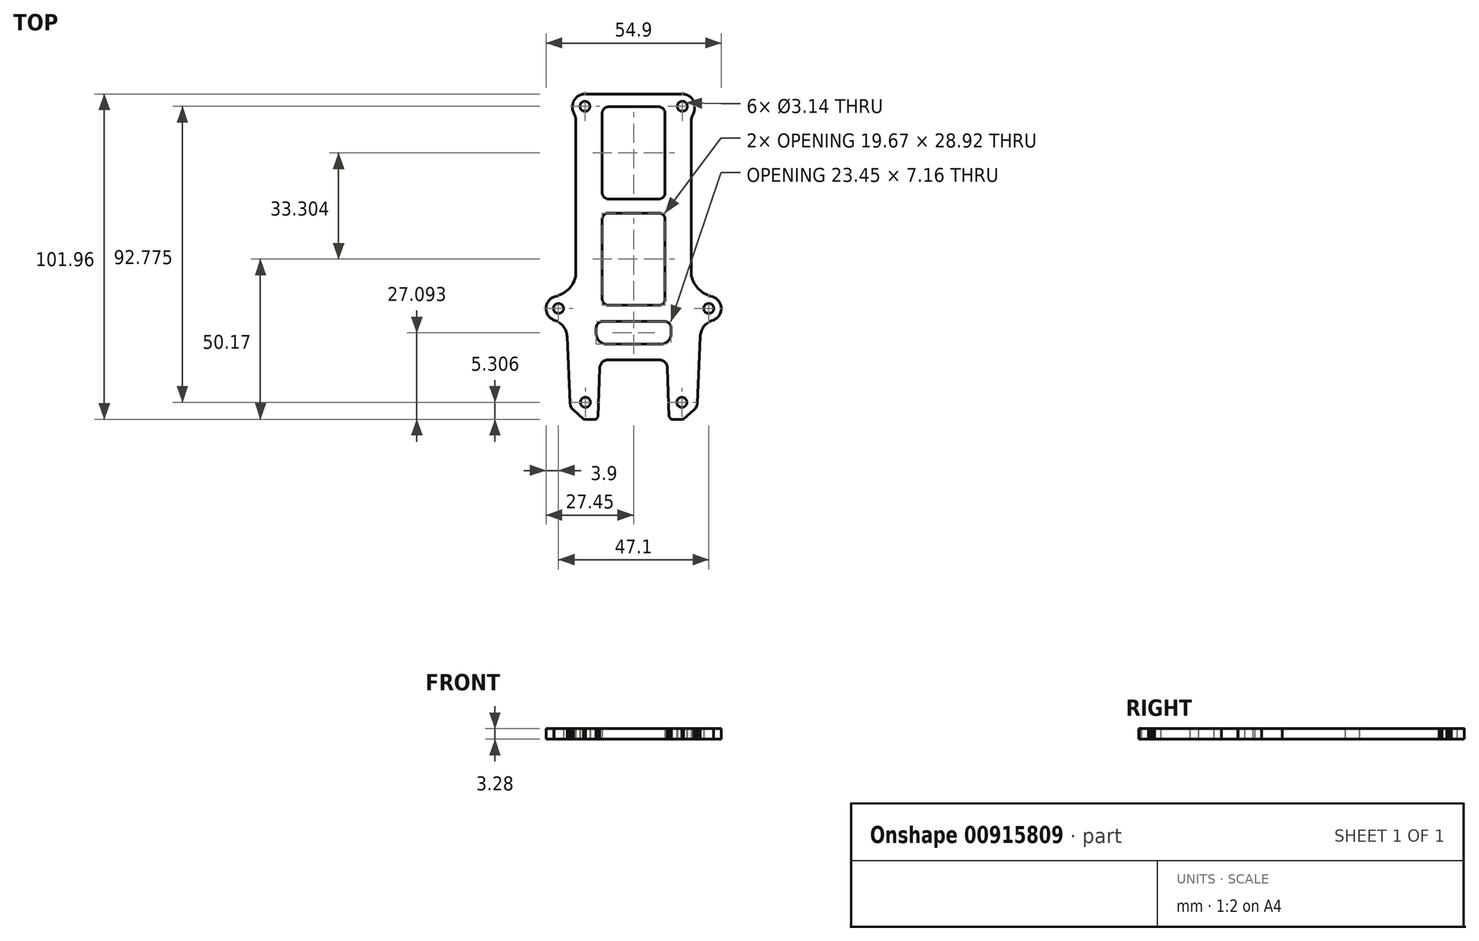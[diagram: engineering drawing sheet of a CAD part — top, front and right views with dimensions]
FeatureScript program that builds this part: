
annotation { "Feature Type Name" : "Feature", "Feature Type Description" : "" }
export const myFeature = defineFeature(function(context is Context, id is Id, definition is map)
    precondition{}
    {
        {
            var Q0;
            Q0=qCreatedBy(makeId("Top.planeOp"),FACE);
            var sketch = newSketch(context, id + "F0", { "sketchPlane" : qUnion([Q0])});
            skLineSegment(sketch, "E0.left", {"start": v(-27.58, 80.06) * mm, "end": v(-27.58, -59.75) * mm});
            skLineSegment(sketch, "E1.bottom", {"start": v(-11.99, 35.27) * mm, "end": v(0, 35.27) * mm});
            skLineSegment(sketch, "E1.top", {"start": v(-11.99, -8.8) * mm, "end": v(0, -8.8) * mm});
            skLineSegment(sketch, "E1.left", {"start": v(-14.99, 32.27) * mm, "end": v(-14.99, -5.8) * mm});
            skPoint(sketch, "E2.visualSharp", {"position": v(-14.99, 36.07) * mm});
            skArc(sketch, "E2.filletArc", {"start": v(-11.99, 35.27) * mm, "mid": v(-14.1, 34.39) * mm, "end": v(-14.99, 32.27) * mm});
            skPoint(sketch, "E3.visualSharp", {"position": v(-14.99, -8.8) * mm});
            skArc(sketch, "E3.filletArc", {"start": v(-14.99, -5.8) * mm, "mid": v(-14.1, -7.92) * mm, "end": v(-11.99, -8.8) * mm});
            skLineSegment(sketch, "E4.bottom", {"start": v(-11.99, 86.01) * mm, "end": v(0, 86.01) * mm});
            skLineSegment(sketch, "E4.top", {"start": v(-11.99, 41.94) * mm, "end": v(0, 41.94) * mm});
            skLineSegment(sketch, "E4.left", {"start": v(-14.99, 83.01) * mm, "end": v(-14.99, 44.94) * mm});
            skPoint(sketch, "E5.visualSharp", {"position": v(-14.99, 86.01) * mm});
            skArc(sketch, "E5.filletArc", {"start": v(-11.99, 86.01) * mm, "mid": v(-14.1, 85.13) * mm, "end": v(-14.99, 83.01) * mm});
            skPoint(sketch, "E6.visualSharp", {"position": v(-14.99, 41.94) * mm});
            skArc(sketch, "E6.filletArc", {"start": v(-14.99, 44.94) * mm, "mid": v(-14.1, 42.82) * mm, "end": v(-11.99, 41.94) * mm});
            skLineSegment(sketch, "E7.bottom", {"start": v(-12.87, -27.38) * mm, "end": v(0, -27.38) * mm});
            skLineSegment(sketch, "E7.top", {"start": v(-14.87, -16.48) * mm, "end": v(0, -16.48) * mm});
            skLineSegment(sketch, "E7.left", {"start": v(-17.87, -22.38) * mm, "end": v(-17.87, -19.48) * mm});
            skPoint(sketch, "E8.visualSharp", {"position": v(-17.87, -16.48) * mm});
            skArc(sketch, "E8.filletArc", {"start": v(-14.87, -16.48) * mm, "mid": v(-16.99, -17.36) * mm, "end": v(-17.87, -19.48) * mm});
            skPoint(sketch, "E9.visualSharp", {"position": v(-17.87, -27.38) * mm});
            skArc(sketch, "E9.filletArc", {"start": v(-17.87, -22.38) * mm, "mid": v(-16.4, -25.92) * mm, "end": v(-12.87, -27.38) * mm});
            skLineSegment(sketch, "E10.bottom", {"start": v(-12.18, -34.84) * mm, "end": v(0, -34.84) * mm});
            skPoint(sketch, "E11.visualSharp", {"position": v(-16.18, -34.84) * mm});
            skArc(sketch, "E11.filletArc", {"start": v(-12.18, -34.84) * mm, "mid": v(-15, -36.01) * mm, "end": v(-16.18, -38.84) * mm});
            skLineSegment(sketch, "E12", {"start": v(-16.18, -38.84) * mm, "end": v(-16.96, -62.01) * mm});
            skLineSegment(sketch, "E13", {"start": v(-16.96, -62.01) * mm, "end": v(-17.99, -63.22) * mm});
            skLineSegment(sketch, "E14", {"start": v(-17.99, -63.22) * mm, "end": v(-23, -63.22) * mm});
            skLineSegment(sketch, "E15", {"start": v(-23, -63.22) * mm, "end": v(-23.9, -63.02) * mm});
            skLineSegment(sketch, "E16", {"start": v(-23.9, -63.02) * mm, "end": v(-28.85, -58.61) * mm});
            skCircle(sketch, "E17", {"center": v(-23.01, -55.13) * mm, "radius": 2.4 * mm});
            skCircle(sketch, "E18", {"center": v(-35.88, -10.3) * mm, "radius": 5.94 * mm});
            skCircle(sketch, "E19", {"center": v(-35.88, -10.3) * mm, "radius": 2.4 * mm});
            skLineSegment(sketch, "E20", {"start": v(-31.78, -23.86) * mm, "end": v(-30.39, -55.6) * mm});
            skLineSegment(sketch, "E21", {"start": v(-30.39, -55.6) * mm, "end": v(-30.18, -56.73) * mm});
            skLineSegment(sketch, "E22", {"start": v(-30.18, -56.73) * mm, "end": v(-29.54, -57.98) * mm});
            skLineSegment(sketch, "E23", {"start": v(-29.54, -57.98) * mm, "end": v(-28.85, -58.61) * mm});
            skArc(sketch, "E24", {"start": v(-31.78, -23.86) * mm, "mid": v(-33.62, -18.8) * mm, "end": v(-38.1, -15.81) * mm});
            skArc(sketch, "E25", {"start": v(-37.74, -4.66) * mm, "mid": v(-31.18, -1.19) * mm, "end": v(-27.58, 5.3) * mm});
            skCircle(sketch, "E26", {"center": v(-23.25, 86.23) * mm, "radius": 2.4 * mm});
            skCircle(sketch, "E27", {"center": v(-23.25, 86.23) * mm, "radius": 5.9 * mm});
            skLineSegment(sketch, "E28", {"start": v(-29.15, 86) * mm, "end": v(-29.15, 84.6) * mm});
            skLineSegment(sketch, "E29", {"start": v(-29.15, 84.6) * mm, "end": v(-28.88, 83.73) * mm});
            skLineSegment(sketch, "E30", {"start": v(-28.88, 83.73) * mm, "end": v(-28.4, 82.67) * mm});
            skLineSegment(sketch, "E31", {"start": v(-28.4, 82.67) * mm, "end": v(-27.86, 81.45) * mm});
            skLineSegment(sketch, "E32", {"start": v(-27.86, 81.45) * mm, "end": v(-27.58, 80.06) * mm});
            skLineSegment(sketch, "E33", {"start": v(-23.2, 92.14) * mm, "end": v(0, 92.14) * mm});
            skPoint(sketch, "E34.startSnap0", {"position": v(0.34, 86.01) * mm});
            skLineSegment(sketch, "E35.right", {"start": v(0, 92.14) * mm, "end": v(0, 86.01) * mm});
            skLineSegment(sketch, "E36.trimOffspring", {"start": v(0, 41.94) * mm, "end": v(0, 35.27) * mm});
            skLineSegment(sketch, "E37.trimOffspring", {"start": v(0, -8.8) * mm, "end": v(0, -16.48) * mm});
            skLineSegment(sketch, "E38.trimOffspring", {"start": v(0, -27.38) * mm, "end": v(0, -34.84) * mm});
            skSolve(sketch);
        }
        {
            var Q0;
            {var subQ8=sQuery(id+"F0.wireOp",EDGE,"E0.right");Q0=makeQuery(id+"F0.imprint","IMPRINT",FACE,{"disambiguationData":[TD([[makeQuery(id+"F0.imprint","IMPRINT",EDGE,{"derivedFrom":subQ8}),-1.0]])]});}
            var Q1;
            {var subQ3=sQuery(id+"F0.wireOp",EDGE,"E0.bottom");var subQ5=sQuery(id+"F0.wireOp",EDGE,"E26");var subQ6=makeQuery(id+"F0.imprint","INTERSECT",VERTEX,{"disambiguationData":[OD(0.0)],"derivedFrom":[subQ3,subQ5]});Q1=makeQuery(id+"F0.imprint","IMPRINT",FACE,{"disambiguationData":[TD([[makeQuery(id+"F0.imprint","IMPRINT",EDGE,{"disambiguationData":[TD([[subQ6,1.0]])],"derivedFrom":subQ5}),-1.0]])]});}
            var Q2;
            {var subQ4=sQuery(id+"F0.wireOp",EDGE,"E21");Q2=makeQuery(id+"F0.imprint","IMPRINT",FACE,{"disambiguationData":[TD([[makeQuery(id+"F0.imprint","IMPRINT",EDGE,{"derivedFrom":subQ4}),1.0]])]});}
            var Q3;
            Q3=makeQuery(id+"F0.imprint","IMPRINT",FACE,{"disambiguationData":[TD([[makeQuery(id+"F0.imprint","IMPRINT",EDGE,{"derivedFrom":sQuery(id+"F0.wireOp",EDGE,"E19")}),-1.0]])]});
            var Q4;
            {var subQ5=sQuery(id+"F0.wireOp",EDGE,"E33");Q4=makeQuery(id+"F0.imprint","IMPRINT",FACE,{"disambiguationData":[TD([[makeQuery(id+"F0.imprint","IMPRINT",EDGE,{"derivedFrom":subQ5}),-1.0]])]});}
            var Q5;
            {var subQ0=sQuery(id+"F0.wireOp",EDGE,"E25");var subQ1=sQuery(id+"F0.wireOp",EDGE,"E0.left");var subQ2=makeQuery(id+"F0.imprint","INTERSECT",VERTEX,{"disambiguationData":[OD(0.0)],"derivedFrom":[subQ1,subQ0]});Q5=makeQuery(id+"F0.imprint","IMPRINT",FACE,{"disambiguationData":[TD([[makeQuery(id+"F0.imprint","IMPRINT",EDGE,{"disambiguationData":[TD([[subQ2,-1.0]])],"derivedFrom":subQ1}),1.0]])]});}
            extrude(context, id + "F1", {"entities" : qUnion([Q0, Q1, Q2, Q3, Q4, Q5]), "depth" : 5 * mm, "offsetDistance" : 25 * mm});
        }
        {
            var Q0;
            Q0=makeQuery(id+"F1.opExtrude","SWEPT_BODY",BODY,{"disambiguationData":[OSD([sQuery(id+"F0.wireOp",EDGE,"E0.left"),sQuery(id+"F0.wireOp",EDGE,"E1.bottom"),sQuery(id+"F0.wireOp",EDGE,"E1.top"),sQuery(id+"F0.wireOp",EDGE,"E1.left"),sQuery(id+"F0.wireOp",EDGE,"E2.filletArc"),sQuery(id+"F0.wireOp",EDGE,"E3.filletArc"),sQuery(id+"F0.wireOp",EDGE,"E4.bottom"),sQuery(id+"F0.wireOp",EDGE,"E4.top"),sQuery(id+"F0.wireOp",EDGE,"E4.left"),sQuery(id+"F0.wireOp",EDGE,"E5.filletArc"),sQuery(id+"F0.wireOp",EDGE,"E6.filletArc"),sQuery(id+"F0.wireOp",EDGE,"E7.bottom"),sQuery(id+"F0.wireOp",EDGE,"E7.top"),sQuery(id+"F0.wireOp",EDGE,"E7.left"),sQuery(id+"F0.wireOp",EDGE,"E8.filletArc"),sQuery(id+"F0.wireOp",EDGE,"E9.filletArc"),sQuery(id+"F0.wireOp",EDGE,"E10.bottom"),sQuery(id+"F0.wireOp",EDGE,"E11.filletArc"),sQuery(id+"F0.wireOp",EDGE,"E12"),sQuery(id+"F0.wireOp",EDGE,"E13"),sQuery(id+"F0.wireOp",EDGE,"E14"),sQuery(id+"F0.wireOp",EDGE,"E15"),sQuery(id+"F0.wireOp",EDGE,"E16"),sQuery(id+"F0.wireOp",EDGE,"E17"),sQuery(id+"F0.wireOp",EDGE,"E18"),sQuery(id+"F0.wireOp",EDGE,"E19"),sQuery(id+"F0.wireOp",EDGE,"E20"),sQuery(id+"F0.wireOp",EDGE,"E21"),sQuery(id+"F0.wireOp",EDGE,"E22"),sQuery(id+"F0.wireOp",EDGE,"E23"),sQuery(id+"F0.wireOp",EDGE,"E24"),sQuery(id+"F0.wireOp",EDGE,"E25"),sQuery(id+"F0.wireOp",EDGE,"E26"),sQuery(id+"F0.wireOp",EDGE,"E27"),sQuery(id+"F0.wireOp",EDGE,"E28"),sQuery(id+"F0.wireOp",EDGE,"E29"),sQuery(id+"F0.wireOp",EDGE,"E30"),sQuery(id+"F0.wireOp",EDGE,"E31"),sQuery(id+"F0.wireOp",EDGE,"E32"),sQuery(id+"F0.wireOp",EDGE,"E33"),sQuery(id+"F0.wireOp",EDGE,"E35.right"),sQuery(id+"F0.wireOp",EDGE,"E36.trimOffspring"),sQuery(id+"F0.wireOp",EDGE,"E37.trimOffspring"),sQuery(id+"F0.wireOp",EDGE,"E38.trimOffspring")])]});
            var Q1;
            Q1=qCreatedBy(makeId("Right.planeOp"),FACE);
            mirror(context, id + "F2", {"operationType" : NewBodyOperationType.ADD, "entities" : qUnion([Q0]), "mirrorPlane" : qUnion([Q1])});
        }
        {
            var Q0;
            Q0=makeQuery(id+"F1.opExtrude","SWEPT_BODY",BODY,{"disambiguationData":[OSD([sQuery(id+"F0.wireOp",EDGE,"E0.left"),sQuery(id+"F0.wireOp",EDGE,"E1.bottom"),sQuery(id+"F0.wireOp",EDGE,"E1.top"),sQuery(id+"F0.wireOp",EDGE,"E1.left"),sQuery(id+"F0.wireOp",EDGE,"E2.filletArc"),sQuery(id+"F0.wireOp",EDGE,"E3.filletArc"),sQuery(id+"F0.wireOp",EDGE,"E4.bottom"),sQuery(id+"F0.wireOp",EDGE,"E4.top"),sQuery(id+"F0.wireOp",EDGE,"E4.left"),sQuery(id+"F0.wireOp",EDGE,"E5.filletArc"),sQuery(id+"F0.wireOp",EDGE,"E6.filletArc"),sQuery(id+"F0.wireOp",EDGE,"E7.bottom"),sQuery(id+"F0.wireOp",EDGE,"E7.top"),sQuery(id+"F0.wireOp",EDGE,"E7.left"),sQuery(id+"F0.wireOp",EDGE,"E8.filletArc"),sQuery(id+"F0.wireOp",EDGE,"E9.filletArc"),sQuery(id+"F0.wireOp",EDGE,"E10.bottom"),sQuery(id+"F0.wireOp",EDGE,"E11.filletArc"),sQuery(id+"F0.wireOp",EDGE,"E12"),sQuery(id+"F0.wireOp",EDGE,"E13"),sQuery(id+"F0.wireOp",EDGE,"E14"),sQuery(id+"F0.wireOp",EDGE,"E15"),sQuery(id+"F0.wireOp",EDGE,"E16"),sQuery(id+"F0.wireOp",EDGE,"E17"),sQuery(id+"F0.wireOp",EDGE,"E18"),sQuery(id+"F0.wireOp",EDGE,"E19"),sQuery(id+"F0.wireOp",EDGE,"E20"),sQuery(id+"F0.wireOp",EDGE,"E21"),sQuery(id+"F0.wireOp",EDGE,"E22"),sQuery(id+"F0.wireOp",EDGE,"E23"),sQuery(id+"F0.wireOp",EDGE,"E24"),sQuery(id+"F0.wireOp",EDGE,"E25"),sQuery(id+"F0.wireOp",EDGE,"E26"),sQuery(id+"F0.wireOp",EDGE,"E27"),sQuery(id+"F0.wireOp",EDGE,"E28"),sQuery(id+"F0.wireOp",EDGE,"E29"),sQuery(id+"F0.wireOp",EDGE,"E30"),sQuery(id+"F0.wireOp",EDGE,"E31"),sQuery(id+"F0.wireOp",EDGE,"E32"),sQuery(id+"F0.wireOp",EDGE,"E33"),sQuery(id+"F0.wireOp",EDGE,"E35.right"),sQuery(id+"F0.wireOp",EDGE,"E36.trimOffspring"),sQuery(id+"F0.wireOp",EDGE,"E37.trimOffspring"),sQuery(id+"F0.wireOp",EDGE,"E38.trimOffspring")])]});
            var Q1;
            Q1=sQuery(id+"F0.wireOp",VERTEX,"E1.top.end");
            transform(context, id + "F3", {"entities" : qUnion([Q0]), "transformType" : TransformType.SCALE_UNIFORMLY, "scale" : 0.66, "scalePoint" : qUnion([Q1]), "makeCopy" : false});
        }
    });
